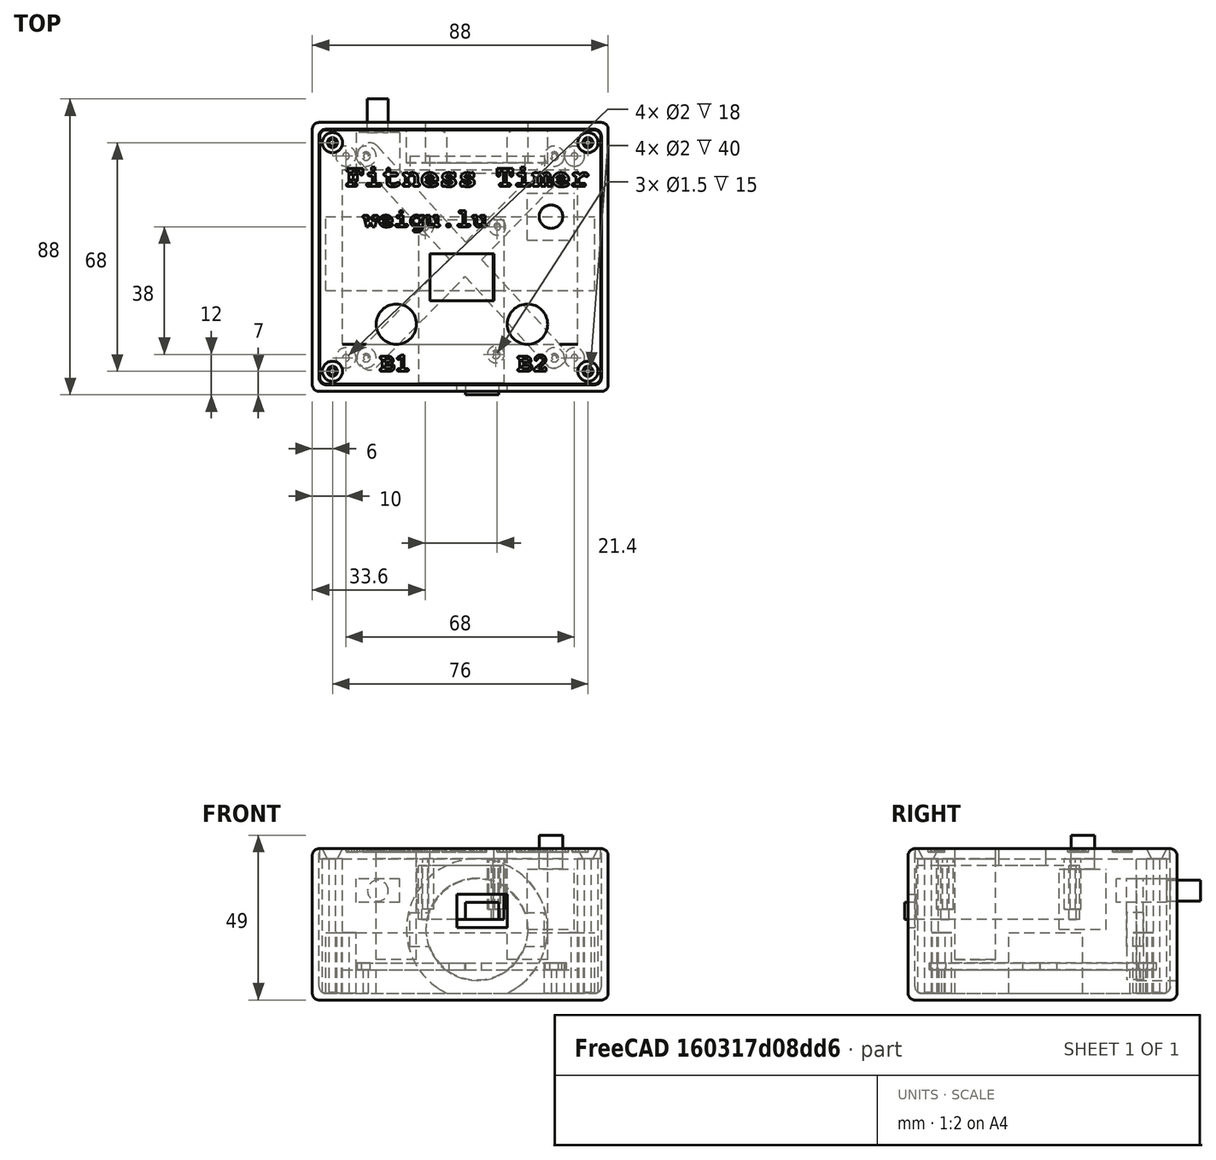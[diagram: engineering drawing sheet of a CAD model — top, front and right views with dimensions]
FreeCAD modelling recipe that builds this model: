
FCSTD DOCUMENT  (FreeCAD 0.19R24276 (Git))
Label: fitness_timer
License: Creative Commons Attribution-NonCommercial-ShareAlike
LicenseURL: http://creativecommons.org/licenses/by-nc-sa/4.0/
objects: Part::Cylinder×51, Part::Cut×40, Part::Box×18, Part::MultiFuse×12, Part::Fillet×5, Part::Cone×4, Part::Part2DObjectPython×4, Part::Extrusion×4
note: 138 computed .brp shape members not serialized (recipe doc carries the construction recipe); baked Part::Feature solids carry a one-line shape summary decoded from their .brp

FEATURE [Part::Box] Box  label="Batt1"
  AttacherType = Attacher::AttachEngine3D
  Height = 18
  Length = 80
  Placement = pos=(4,30,2) rot=(0,0,1;0rad)
  Width = 22
FEATURE [Part::Box] Box001  label="Batt2"
  AttacherType = Attacher::AttachEngine3D
  Height = 7
  Length = 70
  Placement = pos=(9,14,2) rot=(0,0,1;0rad)
  Width = 52
FEATURE [Part::Box] Box002  label="Housing1"
  AttacherType = Attacher::AttachEngine3D
  Height = 45
  Length = 88
  Width = 80
FEATURE [Part::Cylinder] Cylinder  label="Butt1"
  Angle = 360
  AttacherType = Attacher::AttachEngine3D
  Height = 33
  Placement = pos=(64,20,12) rot=(0,0,1;0rad)
  Radius = 6
FEATURE [Part::Cylinder] Cylinder001  label="Butt2"
  Angle = 360
  AttacherType = Attacher::AttachEngine3D
  Height = 33
  Placement = pos=(25,20,12) rot=(0,0,1;0rad)
  Radius = 6
FEATURE [Part::Cylinder] Cylinder002  label="Cylinder"
  Angle = 360
  AttacherType = Attacher::AttachEngine3D
  Height = 10
  Placement = pos=(0,3.5,6.5) rot=(0,-1,0;1.5708rad)
  Radius = 3.1
FEATURE [Part::Box] Box003  label="Cube"
  AttacherType = Attacher::AttachEngine3D
  Height = 13
  Length = 15
  Width = 7
FEATURE [Part::MultiFuse] Fusion  label="Switch"
  Placement = pos=(26,77,29) rot=(0.57735,-0.57735,-0.57735;2.0944rad)
  Shapes = -> [Cylinder002,Box003]
FEATURE [Part::Box] Box004  label="Cube001"
  AttacherType = Attacher::AttachEngine3D
  Height = 18
  Length = 14
  Width = 14
FEATURE [Part::Cylinder] Cylinder003
  Angle = 360
  AttacherType = Attacher::AttachEngine3D
  Height = 10
  Placement = pos=(7,7,18) rot=(0,0,1;0rad)
  Radius = 3.5
FEATURE [Part::MultiFuse] Fusion001  label="Rotary"
  Placement = pos=(64,45,21) rot=(0,0,1;0rad)
  Shapes = -> [Cylinder003,Box004]
FEATURE [Part::Box] Box005  label="Cube002"
  AttacherType = Attacher::AttachEngine3D
  Height = 2
  Length = 19
  Placement = pos=(3.2,10,16) rot=(0,0,1;0rad)
  Width = 14
FEATURE [Part::Box] Box006  label="D1_mini_pro_1"
  AttacherType = Attacher::AttachEngine3D
  Height = 16
  Length = 25.4
  Width = 48.5
FEATURE [Part::Cylinder] Cylinder004
  Angle = 360
  AttacherType = Attacher::AttachEngine3D
  Height = 16
  Placement = pos=(2,2,0) rot=(0,0,1;0rad)
  Radius = 1.05
FEATURE [Part::Cylinder] Cylinder005
  Angle = 360
  AttacherType = Attacher::AttachEngine3D
  Height = 16
  Placement = pos=(23.4,2,0) rot=(0,0,1;0rad)
  Radius = 1.05
FEATURE [Part::Cut] Cut
  Base = -> Box006
  Tool = -> Cylinder004
FEATURE [Part::Cut] Cut001
  Base = -> Cut
  Tool = -> Cylinder005
FEATURE [Part::Box] Box007  label="Cube003"
  AttacherType = Attacher::AttachEngine3D
  Height = 5
  Length = 10
  Placement = pos=(1.5,48,0) rot=(0,0,1;0rad)
  Width = 4
FEATURE [Part::MultiFuse] Fusion002
  Shapes = -> [Box005,Cut001]
FEATURE [Part::MultiFuse] Fusion003
  Shapes = -> [Fusion002,Box007]
FEATURE [Part::Cylinder] Cylinder006
  Angle = 360
  AttacherType = Attacher::AttachEngine3D
  Height = 16
  Placement = pos=(2.4,40,0) rot=(0,0,1;0rad)
  Radius = 1.25
FEATURE [Part::Cut] Cut002  label="D1_mini_pro"
  Base = -> Fusion003
  Placement = pos=(57,51,24) rot=(0,0,1;3.14159rad)
  Tool = -> Cylinder006
FEATURE [Part::Cylinder] Cylinder007  label="speaker"
  Angle = 360
  AttacherType = Attacher::AttachEngine3D
  Height = 5
  Radius = 15
FEATURE [Part::Box] Box008  label="Cube004"
  AttacherType = Attacher::AttachEngine3D
  Height = 5
  Length = 40
  Placement = pos=(-20,-5,0) rot=(0,0,1;0rad)
  Width = 10
FEATURE [Part::MultiFuse] Fusion004  label="Speaker"
  Placement = pos=(49,70,21) rot=(1,0,0;1.5708rad)
  Shapes = -> [Cylinder007,Box008]
FEATURE [Part::Box] Box009  label="Housing001"
  AttacherType = Attacher::AttachEngine3D
  Height = 45
  Length = 84
  Placement = pos=(2,2,2) rot=(0,0,1;0rad)
  Width = 76
FEATURE [Part::Fillet] Fillet
  Base = -> Box002
  Edges = 12 edges r=2: [Edge1,Edge2,Edge3,Edge4,Edge5,Edge6,Edge7,Edge8,Edge9,Edge10,Edge11,Edge12]
FEATURE [Part::Fillet] Fillet001
  Base = -> Box009
  Edges = 12 edges r=2: [Edge1,Edge2,Edge3,Edge4,Edge5,Edge6,Edge7,Edge8,Edge9,Edge10,Edge11,Edge12]
FEATURE [Part::Cut] Cut003  label="Housing3"
  Base = -> Fillet
  Tool = -> Fillet001
FEATURE [Part::Cylinder] Cylinder008
  Angle = 360
  AttacherType = Attacher::AttachEngine3D
  Height = 18
  Placement = pos=(0,0,2) rot=(0,0,1;0rad)
  Radius = 3
FEATURE [Part::Cylinder] Cylinder009
  Angle = 360
  AttacherType = Attacher::AttachEngine3D
  Height = 18
  Placement = pos=(0,0,2) rot=(0,0,1;0rad)
  Radius = 1
FEATURE [Part::Cut] Cut004  label="dist_1"
  Base = -> Cylinder008
  Placement = pos=(10,10,0) rot=(0,0,1;0rad)
  Tool = -> Cylinder009
FEATURE [Part::Cylinder] Cylinder010
  Angle = 360
  AttacherType = Attacher::AttachEngine3D
  Height = 18
  Placement = pos=(0,0,2) rot=(0,0,1;0rad)
  Radius = 3
FEATURE [Part::Cylinder] Cylinder011
  Angle = 360
  AttacherType = Attacher::AttachEngine3D
  Height = 18
  Placement = pos=(0,0,2) rot=(0,0,1;0rad)
  Radius = 1
FEATURE [Part::Cut] Cut005  label="dist_002"
  Base = -> Cylinder010
  Placement = pos=(78,10,0) rot=(0,0,1;0rad)
  Tool = -> Cylinder011
FEATURE [Part::Cylinder] Cylinder012
  Angle = 360
  AttacherType = Attacher::AttachEngine3D
  Height = 18
  Placement = pos=(0,0,2) rot=(0,0,1;0rad)
  Radius = 3
FEATURE [Part::Cylinder] Cylinder013
  Angle = 360
  AttacherType = Attacher::AttachEngine3D
  Height = 18
  Placement = pos=(0,0,2) rot=(0,0,1;0rad)
  Radius = 1
FEATURE [Part::Cut] Cut006  label="dist_003"
  Base = -> Cylinder012
  Placement = pos=(78,70,0) rot=(0,0,1;0rad)
  Tool = -> Cylinder013
FEATURE [Part::Cylinder] Cylinder014
  Angle = 360
  AttacherType = Attacher::AttachEngine3D
  Height = 18
  Placement = pos=(0,0,2) rot=(0,0,1;0rad)
  Radius = 3
FEATURE [Part::Cylinder] Cylinder015
  Angle = 360
  AttacherType = Attacher::AttachEngine3D
  Height = 18
  Placement = pos=(0,0,2) rot=(0,0,1;0rad)
  Radius = 1
FEATURE [Part::Cut] Cut007  label="dist_004"
  Base = -> Cylinder014
  Placement = pos=(10,70,0) rot=(0,0,1;0rad)
  Tool = -> Cylinder015
FEATURE [Part::Cylinder] Cylinder016
  Angle = 360
  AttacherType = Attacher::AttachEngine3D
  Height = 7
  Placement = pos=(0,0,2) rot=(0,0,1;0rad)
  Radius = 3
FEATURE [Part::Cylinder] Cylinder017
  Angle = 360
  AttacherType = Attacher::AttachEngine3D
  Height = 7
  Placement = pos=(0,0,2) rot=(0,0,1;0rad)
  Radius = 0.75
FEATURE [Part::Cut] Cut008  label="dist_005"
  Base = -> Cylinder016
  Placement = pos=(16,10,0) rot=(0,0,1;0rad)
  Tool = -> Cylinder017
FEATURE [Part::Cylinder] Cylinder018
  Angle = 360
  AttacherType = Attacher::AttachEngine3D
  Height = 7
  Placement = pos=(0,0,2) rot=(0,0,1;0rad)
  Radius = 3
FEATURE [Part::Cylinder] Cylinder019
  Angle = 360
  AttacherType = Attacher::AttachEngine3D
  Height = 7
  Placement = pos=(0,0,2) rot=(0,0,1;0rad)
  Radius = 0.75
FEATURE [Part::Cut] Cut009  label="dist_006"
  Base = -> Cylinder018
  Placement = pos=(16,70,0) rot=(0,0,1;0rad)
  Tool = -> Cylinder019
FEATURE [Part::Cylinder] Cylinder020
  Angle = 360
  AttacherType = Attacher::AttachEngine3D
  Height = 7
  Placement = pos=(0,0,2) rot=(0,0,1;0rad)
  Radius = 3
FEATURE [Part::Cylinder] Cylinder021
  Angle = 360
  AttacherType = Attacher::AttachEngine3D
  Height = 7
  Placement = pos=(0,0,2) rot=(0,0,1;0rad)
  Radius = 0.75
FEATURE [Part::Cut] Cut010  label="dist_007"
  Base = -> Cylinder020
  Placement = pos=(72,10,0) rot=(0,0,1;0rad)
  Tool = -> Cylinder021
FEATURE [Part::Cylinder] Cylinder022
  Angle = 360
  AttacherType = Attacher::AttachEngine3D
  Height = 7
  Placement = pos=(0,0,2) rot=(0,0,1;0rad)
  Radius = 3
FEATURE [Part::Cylinder] Cylinder023
  Angle = 360
  AttacherType = Attacher::AttachEngine3D
  Height = 7
  Placement = pos=(0,0,2) rot=(0,0,1;0rad)
  Radius = 0.75
FEATURE [Part::Cut] Cut011  label="dist_008"
  Base = -> Cylinder022
  Placement = pos=(72,70,0) rot=(0,0,1;0rad)
  Tool = -> Cylinder023
FEATURE [Part::Cylinder] Cylinder024
  Angle = 360
  AttacherType = Attacher::AttachEngine3D
  Height = 40
  Placement = pos=(0,0,2) rot=(0,0,1;0rad)
  Radius = 3
FEATURE [Part::Cylinder] Cylinder025
  Angle = 360
  AttacherType = Attacher::AttachEngine3D
  Height = 40
  Placement = pos=(0,0,2) rot=(0,0,1;0rad)
  Radius = 1
FEATURE [Part::Cut] Cut012  label="dist_009"
  Base = -> Cylinder024
  Placement = pos=(6,6,0) rot=(0,0,1;0rad)
  Tool = -> Cylinder025
FEATURE [Part::Cylinder] Cylinder026
  Angle = 360
  AttacherType = Attacher::AttachEngine3D
  Height = 40
  Placement = pos=(0,0,2) rot=(0,0,1;0rad)
  Radius = 3
FEATURE [Part::Cylinder] Cylinder027
  Angle = 360
  AttacherType = Attacher::AttachEngine3D
  Height = 40
  Placement = pos=(0,0,2) rot=(0,0,1;0rad)
  Radius = 1
FEATURE [Part::Cut] Cut013  label="dist_010"
  Base = -> Cylinder026
  Placement = pos=(82,6,0) rot=(0,0,1;0rad)
  Tool = -> Cylinder027
FEATURE [Part::Cylinder] Cylinder028
  Angle = 360
  AttacherType = Attacher::AttachEngine3D
  Height = 40
  Placement = pos=(0,0,2) rot=(0,0,1;0rad)
  Radius = 3
FEATURE [Part::Cylinder] Cylinder029
  Angle = 360
  AttacherType = Attacher::AttachEngine3D
  Height = 40
  Placement = pos=(0,0,2) rot=(0,0,1;0rad)
  Radius = 1
FEATURE [Part::Cut] Cut014  label="dist_011"
  Base = -> Cylinder028
  Placement = pos=(6,74,0) rot=(0,0,1;0rad)
  Tool = -> Cylinder029
FEATURE [Part::Cylinder] Cylinder030
  Angle = 360
  AttacherType = Attacher::AttachEngine3D
  Height = 40
  Placement = pos=(0,0,2) rot=(0,0,1;0rad)
  Radius = 3
FEATURE [Part::Cylinder] Cylinder031
  Angle = 360
  AttacherType = Attacher::AttachEngine3D
  Height = 40
  Placement = pos=(0,0,2) rot=(0,0,1;0rad)
  Radius = 1
FEATURE [Part::Cut] Cut015  label="dist_012"
  Base = -> Cylinder030
  Placement = pos=(82,74,0) rot=(0,0,1;0rad)
  Tool = -> Cylinder031
FEATURE [Part::MultiFuse] Fusion005  label="Housing2"
  Shapes = -> [Cut004,Cut005,Cut006,Cut007,Cut008,Cut009,Cut010,Cut011,Cut012,Cut013,Cut014,Cut015,Cut003]
FEATURE [Part::Cylinder] Cylinder032
  Angle = 360
  AttacherType = Attacher::AttachEngine3D
  Height = 10
  Radius = 15.2
FEATURE [Part::Cylinder] Cylinder033
  Angle = 360
  AttacherType = Attacher::AttachEngine3D
  Height = 10
  Radius = 21
FEATURE [Part::Cut] Cut016
  Base = -> Cylinder033
  Placement = pos=(49,68,21) rot=(0.57735,0.57735,0.57735;4.18879rad)
  Tool = -> Cylinder032
FEATURE [Part::Cylinder] Cylinder034
  Angle = 360
  AttacherType = Attacher::AttachEngine3D
  Height = 20
  Placement = pos=(49,68,21) rot=(-1,0,0;1.5708rad)
  Radius = 15.2
FEATURE [Part::MultiFuse] Fusion006
  Shapes = -> [Cut016,Fusion005]
FEATURE [Part::Cut] Cut017
  Base = -> Fusion006
  Tool = -> Cylinder034
FEATURE [Part::Cylinder] Cylinder035
  Angle = 360
  AttacherType = Attacher::AttachEngine3D
  Height = 10
  Placement = pos=(0,3.5,6.5) rot=(0,-1,0;1.5708rad)
  Radius = 3.1
FEATURE [Part::Box] Box010  label="Cube005"
  AttacherType = Attacher::AttachEngine3D
  Height = 13
  Length = 15
  Width = 7
FEATURE [Part::MultiFuse] Fusion007  label="Switch001"
  Placement = pos=(26,77,29) rot=(0.57735,-0.57735,-0.57735;2.0944rad)
  Shapes = -> [Cylinder035,Box010]
FEATURE [Part::Cut] Cut018  label="Housing"
  Base = -> Cut017
  Tool = -> Fusion007
FEATURE [Part::Box] Box011  label="Cube006"
  AttacherType = Attacher::AttachEngine3D
  Height = 3
  Length = 83.6
  Placement = pos=(2.2,2.2,42) rot=(0,0,1;0rad)
  Width = 75.6
FEATURE [Part::Fillet] Fillet002  label="lid2"
  Base = -> Box011
  Edges = 4 edges r=2: [Edge1,Edge3,Edge5,Edge7]
FEATURE [Part::Box] Box012  label="Window"
  AttacherType = Attacher::AttachEngine3D
  Height = 5
  Length = 19
  Placement = pos=(35,27,41) rot=(0,0,1;0rad)
  Width = 14
FEATURE [Part::Cylinder] Cylinder036
  Angle = 360
  AttacherType = Attacher::AttachEngine3D
  Height = 15
  Placement = pos=(54.6,11,39) rot=(0,0,1;0rad)
  Radius = 2.5
FEATURE [Part::Cylinder] Cylinder037
  Angle = 360
  AttacherType = Attacher::AttachEngine3D
  Height = 15
  Placement = pos=(55,49,39) rot=(0,0,1;0rad)
  Radius = 2.5
FEATURE [Part::Cylinder] Cylinder038
  Angle = 360
  AttacherType = Attacher::AttachEngine3D
  Height = 15
  Placement = pos=(33.6,49,39) rot=(0,0,1;0rad)
  Radius = 0.75
FEATURE [Part::Cylinder] Cylinder039
  Angle = 360
  AttacherType = Attacher::AttachEngine3D
  Height = 15
  Placement = pos=(33.6,49,39) rot=(0,0,1;0rad)
  Radius = 2.5
FEATURE [Part::Cylinder] Cylinder040
  Angle = 360
  AttacherType = Attacher::AttachEngine3D
  Height = 15
  Placement = pos=(55,49,39) rot=(0,0,1;0rad)
  Radius = 0.75
FEATURE [Part::Cylinder] Cylinder041
  Angle = 360
  AttacherType = Attacher::AttachEngine3D
  Height = 15
  Placement = pos=(54.6,11,39) rot=(0,0,1;0rad)
  Radius = 0.75
FEATURE [Part::Cut] Cut019
  Base = -> Cylinder036
  Placement = pos=(0,0,-12) rot=(0,0,1;0rad)
  Tool = -> Cylinder041
FEATURE [Part::Cut] Cut020
  Base = -> Cylinder037
  Placement = pos=(0,0,-12) rot=(0,0,1;0rad)
  Tool = -> Cylinder040
FEATURE [Part::Cut] Cut021
  Base = -> Cylinder039
  Placement = pos=(0,0,-12) rot=(0,0,1;0rad)
  Tool = -> Cylinder038
FEATURE [Part::Cylinder] Cylinder042  label="Butt003"
  Angle = 360
  AttacherType = Attacher::AttachEngine3D
  Height = 33
  Placement = pos=(64,20,12) rot=(0,0,1;0rad)
  Radius = 6
FEATURE [Part::Cut] Cut022
  Base = -> Fillet002
  Tool = -> Cylinder042
FEATURE [Part::Cylinder] Cylinder043  label="Butt004"
  Angle = 360
  AttacherType = Attacher::AttachEngine3D
  Height = 33
  Placement = pos=(25,20,12) rot=(0,0,1;0rad)
  Radius = 6
FEATURE [Part::Cut] Cut023
  Base = -> Cut022
  Tool = -> Cylinder043
FEATURE [Part::Cut] Cut024
  Base = -> Cut023
  Tool = -> Box012
FEATURE [Part::Box] Box013  label="Cube007"
  AttacherType = Attacher::AttachEngine3D
  Height = 18
  Length = 14
  Width = 14
FEATURE [Part::Cylinder] Cylinder044
  Angle = 360
  AttacherType = Attacher::AttachEngine3D
  Height = 10
  Placement = pos=(7,7,18) rot=(0,0,1;0rad)
  Radius = 3.5
FEATURE [Part::MultiFuse] Fusion008  label="Rotary001"
  Placement = pos=(64,45,21) rot=(0,0,1;0rad)
  Shapes = -> [Cylinder044,Box013]
FEATURE [Part::Cut] Cut025  label="Lid3"
  Base = -> Cut024
  Tool = -> Fusion008
FEATURE [Part::Box] Box014  label="USB1"
  AttacherType = Attacher::AttachEngine3D
  Height = 10
  Length = 15
  Placement = pos=(43,-1,21.5) rot=(0,0,1;0rad)
  Width = 12
FEATURE [Part::Cut] Cut026
  Base = -> Cut018
  Tool = -> Box014
FEATURE [Part::Cylinder] Cylinder045
  Angle = 360
  AttacherType = Attacher::AttachEngine3D
  Height = 10
  Placement = pos=(0,3.5,6.5) rot=(0,-1,0;1.5708rad)
  Radius = 3.1
FEATURE [Part::Box] Box015  label="Cube008"
  AttacherType = Attacher::AttachEngine3D
  Height = 13
  Length = 15
  Width = 7
FEATURE [Part::MultiFuse] Fusion009  label="Switch002"
  Placement = pos=(26,77,29) rot=(0.57735,-0.57735,-0.57735;2.0944rad)
  Shapes = -> [Cylinder045,Box015]
FEATURE [Part::Cut] Cut027  label="housing"
  Base = -> Cut026
  Tool = -> Fusion009
FEATURE [Part::MultiFuse] Fusion010  label="Lid4"
  Shapes = -> [Cut025,Cut021,Cut020,Cut019]
FEATURE [Part::Cone] Cone
  Angle = 360
  AttacherType = Attacher::AttachEngine3D
  Height = 3
  Placement = pos=(6,6,42) rot=(0,0,1;0rad)
  Radius1 = 1.5
  Radius2 = 3
FEATURE [Part::Cone] Cone001
  Angle = 360
  AttacherType = Attacher::AttachEngine3D
  Height = 3
  Placement = pos=(82,6,42) rot=(0,0,1;0rad)
  Radius1 = 1.5
  Radius2 = 3
FEATURE [Part::Cone] Cone002
  Angle = 360
  AttacherType = Attacher::AttachEngine3D
  Height = 3
  Placement = pos=(82,74,42) rot=(0,0,1;0rad)
  Radius1 = 1.5
  Radius2 = 3
FEATURE [Part::Cone] Cone003
  Angle = 360
  AttacherType = Attacher::AttachEngine3D
  Height = 3
  Placement = pos=(6,74,42) rot=(0,0,1;0rad)
  Radius1 = 1.5
  Radius2 = 3
FEATURE [Part::Cut] Cut028
  Base = -> Fusion010
  Tool = -> Cone
FEATURE [Part::Cut] Cut029
  Base = -> Cut028
  Tool = -> Cone003
FEATURE [Part::Cut] Cut030
  Base = -> Cut029
  Tool = -> Cone002
FEATURE [Part::Cut] Cut031  label="lid3"
  Base = -> Cut030
  Tool = -> Cone001
FEATURE [Part::Part2DObjectPython] ShapeString  # Draft 2D object (typed FeaturePython)
  FontFile = <path>
  Placement = pos=(20,6,45) rot=(0,0,1;0rad)
  Size = 2.5
  String = B1
  Tracking = 0
FEATURE [Part::Part2DObjectPython] ShapeString001  # Draft 2D object (typed FeaturePython)
  FontFile = <path>
  Placement = pos=(61,6,45) rot=(0,0,1;0rad)
  Size = 2.5
  String = B2
  Tracking = 0
FEATURE [Part::Part2DObjectPython] ShapeString002  # Draft 2D object (typed FeaturePython)
  FontFile = <path>
  Placement = pos=(10,61,45) rot=(0,0,1;0rad)
  Size = 3
  String = Fitness Timer
  Tracking = 0
FEATURE [Part::Part2DObjectPython] ShapeString003  # Draft 2D object (typed FeaturePython)
  FontFile = <path>
  Placement = pos=(15,49,45) rot=(0,0,1;0rad)
  Size = 2.5
  String = weigu.lu
  Tracking = 0
FEATURE [Part::Box] Box016  label="Cube009"
  AttacherType = Attacher::AttachEngine3D
  Height = 2
  Length = 88
  Placement = pos=(13.5822,70.241,9) rot=(0,0,-1;0.820305rad)
  Width = 7
FEATURE [Part::Fillet] Fillet003
  Base = -> Box016
  Edges = 4 edges r=3: [Edge1,Edge3,Edge5,Edge7]
  Placement = pos=(-1.92937,0.302387,0) rot=(0,0,-1;0.006981rad)
FEATURE [Part::Box] Box017  label="Cube010"
  AttacherType = Attacher::AttachEngine3D
  Height = 2
  Length = 85
  Placement = pos=(13.5822,70.241,9) rot=(0,0,-1;0.820305rad)
  Width = 7
FEATURE [Part::Fillet] Fillet004
  Base = -> Box017
  Edges = 4 edges r=3: [Edge1,Edge3,Edge5,Edge7]
  Placement = pos=(87.8221,-5.22514,0) rot=(0,0,1;1.61617rad)
FEATURE [Part::Cylinder] Cylinder046
  Angle = 360
  AttacherType = Attacher::AttachEngine3D
  Height = 2
  Placement = pos=(72,70,9) rot=(0,0,1;0rad)
  Radius = 3
FEATURE [Part::MultiFuse] Fusion011
  Shapes = -> [Fillet003,Fillet004,Cylinder046]
FEATURE [Part::Cylinder] Cylinder047
  Angle = 360
  AttacherType = Attacher::AttachEngine3D
  Height = 10
  Placement = pos=(16,10,2) rot=(0,0,1;0rad)
  Radius = 1.25
FEATURE [Part::Cylinder] Cylinder048
  Angle = 360
  AttacherType = Attacher::AttachEngine3D
  Height = 10
  Placement = pos=(72,10,2) rot=(0,0,1;0rad)
  Radius = 1.25
FEATURE [Part::Cylinder] Cylinder049
  Angle = 360
  AttacherType = Attacher::AttachEngine3D
  Height = 10
  Placement = pos=(16,70,2) rot=(0,0,1;0rad)
  Radius = 1.25
FEATURE [Part::Cylinder] Cylinder050
  Angle = 360
  AttacherType = Attacher::AttachEngine3D
  Height = 10
  Placement = pos=(72,70,2) rot=(0,0,1;0rad)
  Radius = 1.25
FEATURE [Part::Cut] Cut032
  Base = -> Fusion011
  Tool = -> Cylinder047
FEATURE [Part::Cut] Cut033
  Base = -> Cut032
  Tool = -> Cylinder050
FEATURE [Part::Cut] Cut034
  Base = -> Cut033
  Tool = -> Cylinder049
FEATURE [Part::Cut] Cut035  label="Batholder2"
  Base = -> Cut034
  Tool = -> Cylinder048
FEATURE [Part::Extrusion] Extrude
  Base = -> ShapeString
  Dir = (0,0,1)
  DirMode = 2
  FaceMakerClass = Part::FaceMakerBullseye
  LengthFwd = 1
  LengthRev = 0
  Placement = pos=(0,0,-1) rot=(0,0,1;0rad)
  Solid = false
  Symmetric = false
FEATURE [Part::Extrusion] Extrude001
  Base = -> ShapeString003
  Dir = (0,0,1)
  DirMode = 2
  FaceMakerClass = Part::FaceMakerBullseye
  LengthFwd = 1
  LengthRev = 0
  Placement = pos=(0,0,-1) rot=(0,0,1;0rad)
  Solid = false
  Symmetric = false
FEATURE [Part::Extrusion] Extrude002
  Base = -> ShapeString002
  Dir = (0,0,1)
  DirMode = 2
  FaceMakerClass = Part::FaceMakerBullseye
  LengthFwd = 1
  LengthRev = 0
  Placement = pos=(0,0,-1) rot=(0,0,1;0rad)
  Solid = false
  Symmetric = false
FEATURE [Part::Extrusion] Extrude003
  Base = -> ShapeString001
  Dir = (0,0,1)
  DirMode = 2
  FaceMakerClass = Part::FaceMakerBullseye
  LengthFwd = 1
  LengthRev = 0
  Placement = pos=(0,0,-1) rot=(0,0,1;0rad)
  Solid = false
  Symmetric = false
FEATURE [Part::Cut] Cut036
  Base = -> Cut031
  Tool = -> Extrude
FEATURE [Part::Cut] Cut037
  Base = -> Cut036
  Tool = -> Extrude003
FEATURE [Part::Cut] Cut038
  Base = -> Cut037
  Tool = -> Extrude002
FEATURE [Part::Cut] Cut039  label="lid"
  Base = -> Cut038
  Tool = -> Extrude001
note: 4 file-system paths scrubbed to <path> (originals preserved in the JSON sidecar)
